# Revit family: HVAC_Fireplaces_Regency-Fireplace_San-Francisco-gas-fireplace_CB60E
name_source: partatom
category: Specialty Equipment
units: mm (PartAtom-declared; Revit-internal decimal feet)

## family parameters
Classification Number = 23.40.20.34.14
Cut with Voids When Loaded = No
Enable Cutting in Views = No
Host = Face
Maintain Annotation Orientation = No
Part Type = Normal
Room Calculation Point = No
Round Connector Dimension = Use Diameter
Shared = No

## types (2) — shared parameters
Apparent Load = 0 VA
Current = 2 A
Depth = 20 "
Description = The Regency City Series San Francisco Bay 60” large gas fireplace is the perfect size for any room. The new San Francisco Bay 60” gas fireplace includes all the innovations of the City Series in an all new size.
Duct Connector Description = 5” Inner /8” Outer
Duct Diameter = 4 "
Frequency = 60 Hz
Gas flow = 0.0 L/s
Height = 39 "
Housing Material = Regency Fireplace - Metal - Black
Manufacturer = Regency Fireplace
Model = CB60E-NG
Nom Vent height = 74 "
Number of Poles = 1
Pipe Diameter = 1 "
Power Consumption = 0 W
Power Factor = 1
Product Documentation Link = https://assets.regency-fire.com
Product Page URL = https://www.regency-fire.com
Product data url = https://www.bimobject.com
URL = https://www.regency-fire.com
Ventilation flow = 0.0 L/s
Voltage = 120 V
WIFI Dongle Installation = Yes
Width = 71 "
zero-valued in all types: Default Elevation, Version

## per-type parameters (varying)
| type | CSA P.4.1 | Fuel Type | Gas Connector Description | Manifold Pressure - High | Manifold Pressure - Low | Maximum Input Altitude 0-4500 ft. (0-1372m) | Minimum Input Altitude 0-4500 ft. (0-1372m) | Minimum Supply Pressure | Orifce Size -Altitude 0-4500 ft |
| CB60E-LP1 | 56.43% | Propane | Propane gas supply | 10.5” W.C. (2.62 kPa) | 2.9” W.C. (0.72 kPa) | 36,000 Btu/h (10.54 kW) | 19,500 Btu/h (5.71 kW) | 11” W.C. (2.73 kPa) | # 50 DMS |
| CB60E-NG1 | 56.23% | Natural Gas | Natural gas supply | 3.8” W.C. (0.94 kPa) | 1.1” W.C. (0.27 kPa) | 39,000 Btu/h (11.42 kW) | 21,000Btu/h (6.15 kW) | 5” W.C. (1.25 kPa) | # 32 DMS |

## geometry (parser evidence)
native form markers: Sweep x5
no freeform markers — native parametric forms only
